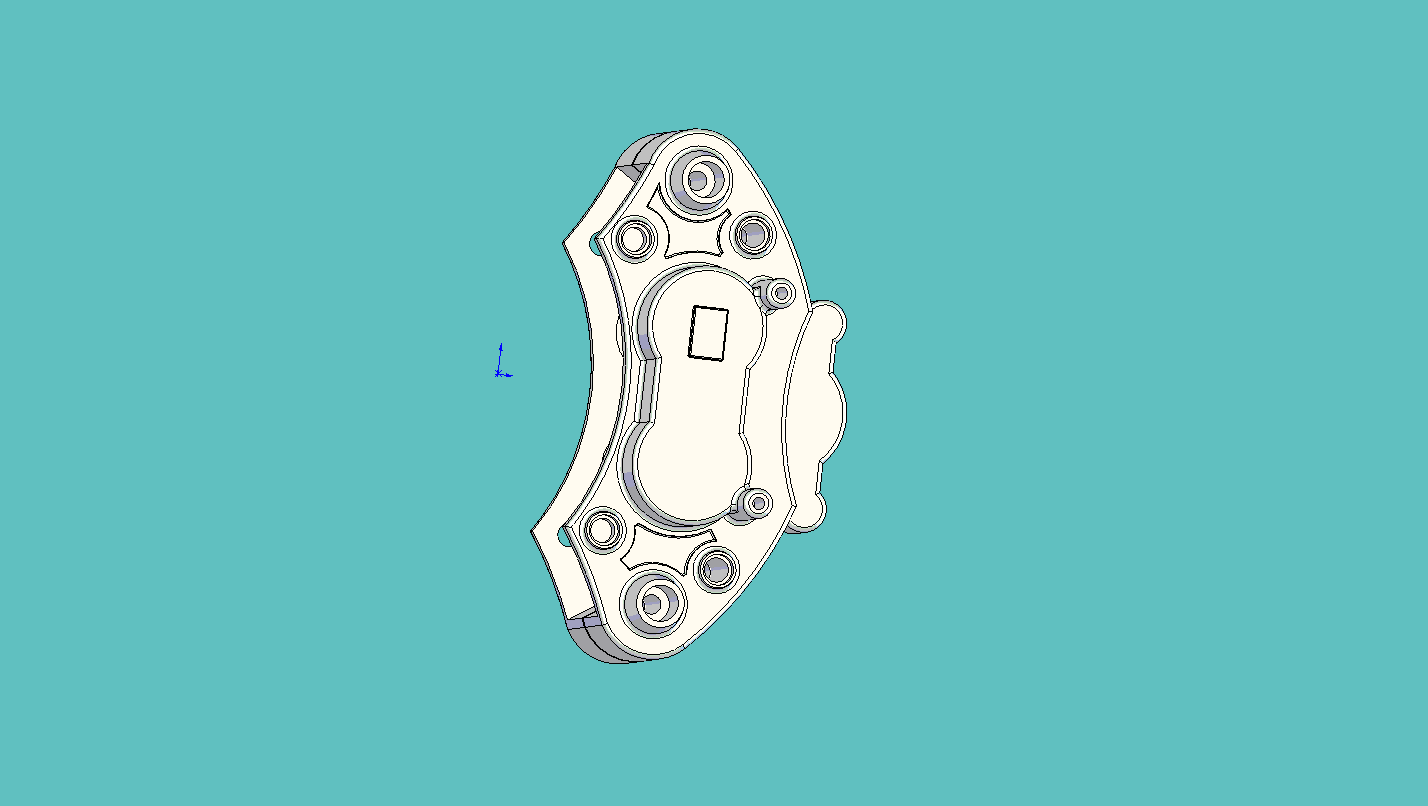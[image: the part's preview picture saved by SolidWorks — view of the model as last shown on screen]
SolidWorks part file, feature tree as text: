
SOLIDWORKS PART (.sldprt)
format: sldprt  version: not decoded by parser v0  size: 2,501,632 bytes
history: native  units: mm
features: sketch x22, cut_extrude x15, fillet x10, extrude x7, plane x2, material x1, chamfer x1, mirror x1 (+13 scaffold rows collapsed)
feature tree (72):
  scaffold x13  (default folders/planes/origin — collapsed)
  material  "Material <not specified>"
  sketch  "Sketch1"  dims[D1=63.5mm]
  extrude  "Extrude1"  Depth=31.75mm
  sketch  "Sketch5"  dims[D1=~43.962388mm]
  extrude  "Extrude2"  Depth=50.8mm
  sketch  "Sketch3"  dims[D1=50.0mm]
  cut_extrude  "Cut-Extrude1"  Depth=25.4mm
  sketch  "Sketch7"  dims[c1.D1=12.7mm c1.D2=12.7mm c2.D1=~13.906952mm c2.D2=25.0mm c2.D3=25.0mm c3.D1=~12.799272mm c3.D3=152.4mm]
  fillet  "Fillet1"  Radius=2.54mm
  fillet  "Fillet2"  Radius=2.54mm
  fillet  "Fillet3"  Radius=2.54mm
  sketch  "Sketch10"
  cut_extrude  "Cut-Extrude3"  [1 undecoded]
  plane  "Plane1"  Offset=10.16mm
  plane  "Plane2"  Offset=8.636mm
  sketch  "Sketch13"  dims[D1=273.05mm D2=137.16mm]
  cut_extrude  "Cut-Extrude4"  [1 undecoded]
  sketch  "Sketch14"
  cut_extrude  "Cut-Extrude5"  [1 undecoded]
  sketch  "Sketch15"
  extrude  "Extrude3"  Depth=53.18mm
  fillet  "Fillet4"  Radius=2.54mm
  sketch  "Sketch16"  dims[D1=~1.636236mm]
  cut_extrude  "Cut-Extrude6"  Depth=27.94mm
  fillet  "Fillet5"  Radius=2.54mm
  sketch  "Sketch17"
  extrude  "Extrude4"  Depth=2.54mm
  fillet  "Fillet6"  Radius=0.508mm
  chamfer  "Chamfer1"  Distance=1.27mm Angle=45deg
  sketch  "Sketch20"  dims[c1.D1=31.75mm c1.D2=25.4mm c2.D1=~20.003376mm]
  extrude  "Extrude5"  Depth=20.32mm
  cut_extrude  "Cut-Extrude8"  [1 undecoded]
  sketch  "Sketch21"  dims[D1=~4.108238mm]
  cut_extrude  "Cut-Extrude10"  Depth=25.4mm
  fillet  "Fillet7"  Radius=2.54mm
  sketch  "Sketch22"  dims[D1=10.16mm]
  cut_extrude  "Cut-Extrude11"  [1 undecoded]
  sketch  "Sketch24"
  cut_extrude  "Cut-Extrude12"  Depth=22.86mm
  sketch  "Sketch25"  dims[D1=20.574mm]
  extrude  "Extrude6"  Depth=5.08mm
  fillet  "Fillet8"  Radius=2.54mm
  sketch  "Sketch27"  dims[D1=~16.253517mm]
  cut_extrude  "Cut-Extrude15"  Depth=5.08mm
  sketch  "Sketch28"
  cut_extrude  "Cut-Extrude16"  Depth=2.54mm
  fillet  "Fillet9"  Radius=0.762mm
  mirror  "Mirror1"
  sketch  "Sketch29"  dims[D1=7.62mm]
  extrude  "Extrude7"  [1 undecoded]
  sketch  "Sketch30"
  sketch  "Sketch31"  dims[D1=5.08mm]
  cut_extrude  "Cut-Extrude18"  Depth=16.392582mm
  sketch  "Sketch32"  dims[D1=8.89mm]
  cut_extrude  "Cut-Extrude19"  Depth=16.392582mm
  cut_extrude  "Cut-Extrude20"  Depth=43.688mm
  sketch  "Sketch33"
  cut_extrude  "Cut-Extrude21"  Depth=59.69mm
  fillet  "Fillet11"  Radius=2.54mm
decode coverage: 41 of 56 modeling features carry decoded parameters
note: ~ marks probable driven/reference dimensions
note: 6 parameter values undecoded
summary: no parameter record found for 6 features
note: suppression state not decoded; provenance and decode notes live in map.json
